# Revit family: City Open H K
name_source: partatom
category: Attrezzatura meccanica
units: mm (PartAtom-declared; Revit-internal decimal feet)

## family parameters
Basato su piano di lavoro = No
Classificazione = Nessuno
Condiviso = No
Mantieni orientamento annotazione = No
Punto di calcolo locali = No
Quota connettore circolare = Usa diametro
Sempre verticale = Sì
Taglio con vuoti quando caricato = No
Tipo di parte = Normale

## types (2) — shared parameters
Combustion air inlet - separate system = 80 mm  [stored 0.262467 ft]
Date of publishing = 04/10/2023
Depth = 240 mm  [stored 0.787402 ft]
Domestic Cold Water Diameter = 21 mm  [stored 0.0688976 ft]
Domestic Hot Water Diameter = 21 mm  [stored 0.0688976 ft]
Flue outlet = 100 mm  [stored 0.328084 ft]
Gas Inlet Diameter = 26 mm
Height = 850 mm  [stored 2.78871 ft]
Hydronic Return Diameter = 26 mm
Hydronic Supply Diameter = 26 mm
IFC Classification = Boilers
Manufacturer country = Italy
Manufacturer name = Italtherm S.p.A.
Material main = Metal
Material secondary = Plastic
Omniclass Description = Condensing boilers
Power consumption of eletric heaters (W) Additional = 34 mm
Power supply | Frequency (Hz) = 50 Hz
Power supply | Phase = 1
Power supply | Voltage (V) = 230 V
Product family = Heating
Product group = Thermal unit
Siphon with condensate drain = 25 mm  [stored 0.082021 ft]
Uniclass 2015 Name = Boilers
Width = 520 mm  [stored 1.70604 ft]
zero-valued in all types: Prospetto di default

## per-type parameters (varying)
| type | Efficiency 30% | Maximum heat output 50/30°C | Maximum heat output 80/60°C | Maximum heating heat input | Minimum heat output 50/30°C | Minimum heat output 80/60°C | Nominal efficiency 50/30°C | Nominal efficiency 80/60°C | Power consumption (W) | Weight |
| City Open H 25 K | 106,20% | 22100 W | 20300 W | 21000 W | 2700 W | 2400 W | 105,80% | 95,90% | 75 W | 42,50 kg |
| City Open H 35 K | 106,90% | 29000 W | 26300 W | 28000 W | 3700 W | 3200 W | 105,10% | 95,20% | 107 W | 47,00 kg |

note: [stored X ft] marks values corroborated as IEEE doubles in the binary element streams (Revit-internal decimal feet)
